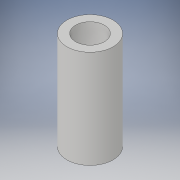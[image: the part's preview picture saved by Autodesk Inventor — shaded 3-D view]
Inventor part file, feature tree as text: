
AUTODESK INVENTOR PART (.ipt)
format: ipt  version: 2018 (Build 220112000, 112)  size: 94,720 bytes
history: native  units: in
note: dims shown in document units (in); Inventor stores cm internally (conversion verified against a paired STEP export)
features: extrude x1, sketch x1
ambient origin geometry x8: Origin, YZ Plane, XZ Plane, XY Plane, X Axis, Y Axis, Z Axis, Center Point
bodies: Solid1 (feature_tree)
feature tree (2):
  extrude  "Extrusion1"  Depth=1.061in
  sketch  "Sketch1"  dims[d0=0.5in d1=0.312in d2=1.061in d3=0.0in]
